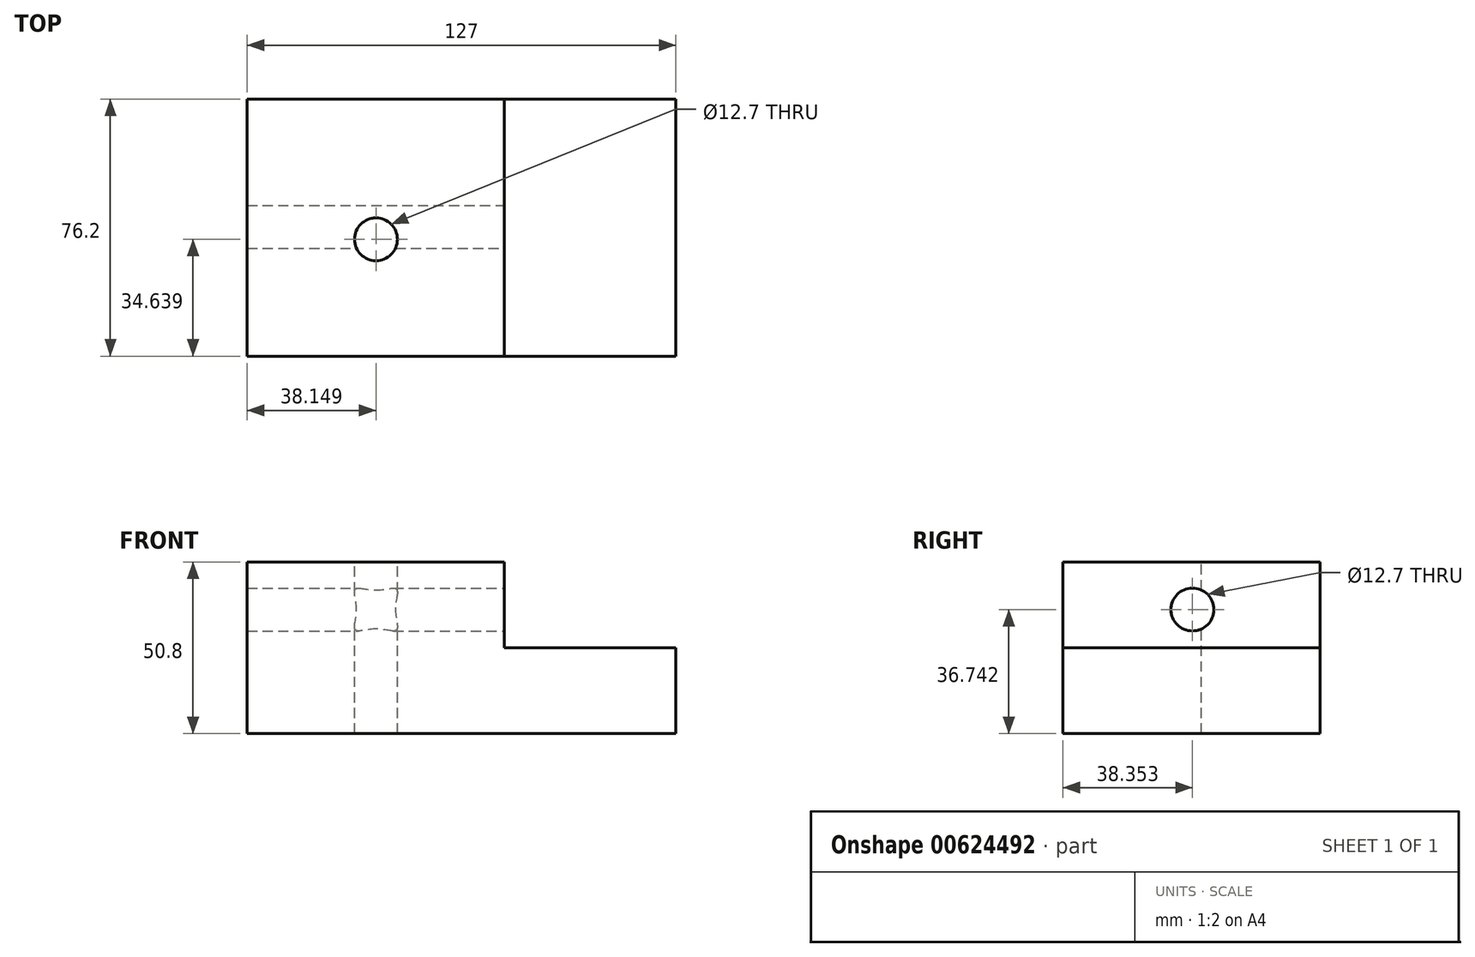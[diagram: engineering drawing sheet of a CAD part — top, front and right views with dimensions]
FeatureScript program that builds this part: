
annotation { "Feature Type Name" : "Feature", "Feature Type Description" : "" }
export const myFeature = defineFeature(function(context is Context, id is Id, definition is map)
    precondition{}
    {
        {
            var Q0;
            Q0=qCreatedBy(makeId("Front.planeOp"),FACE);
            var sketch = newSketch(context, id + "F0", { "sketchPlane" : qUnion([Q0])});
            skLineSegment(sketch, "E0.bottom", {"start": v(0, 0) * mm, "end": v(127, 0) * mm});
            skLineSegment(sketch, "E0.top", {"start": v(0, 50.8) * mm, "end": v(127, 50.8) * mm});
            skLineSegment(sketch, "E0.left", {"start": v(0, 0) * mm, "end": v(0, 50.8) * mm});
            skLineSegment(sketch, "E0.right", {"start": v(127, 0) * mm, "end": v(127, 50.8) * mm});
            skLineSegment(sketch, "E1.bottom", {"start": v(76.2, 50.8) * mm, "end": v(127, 50.8) * mm});
            skLineSegment(sketch, "E1.top", {"start": v(76.2, 25.4) * mm, "end": v(127, 25.4) * mm});
            skLineSegment(sketch, "E1.left", {"start": v(76.2, 50.8) * mm, "end": v(76.2, 25.4) * mm});
            skLineSegment(sketch, "E1.right", {"start": v(127, 50.8) * mm, "end": v(127, 25.4) * mm});
            skSolve(sketch);
        }
        {
            var Q0;
            Q0=makeQuery(id+"F0.imprint","IMPRINT",FACE,{"disambiguationData":[TD([[makeQuery(id+"F0.imprint","IMPRINT",EDGE,{"derivedFrom":sQuery(id+"F0.wireOp",EDGE,"E0.bottom")}),1.0]])]});
            extrude(context, id + "F1", {"entities" : qUnion([Q0]), "depth" : 76.2 * mm, "offsetDistance" : 25.4 * mm});
        }
        {
            var Q0;
            Q0=makeQuery(id+"F1.opExtrude","SWEPT_FACE",FACE,{"disambiguationData":[OSD([sQuery(id+"F0.wireOp",EDGE,"E0.top")])]});
            var sketch = newSketch(context, id + "F2", { "sketchPlane" : qUnion([Q0])});
            skCircle(sketch, "E2", {"center": v(38.15, -41.56) * mm, "radius": 15.37 * mm});
            skSolve(sketch);
        }
        {
            var Q0;
            Q0=sQuery(id+"F2.wireOp",VERTEX,"E2.center");
            var Q1;
            Q1=makeQuery(id+"F1.opExtrude","SWEPT_BODY",BODY,{"disambiguationData":[OSD([sQuery(id+"F0.wireOp",EDGE,"E0.bottom"),sQuery(id+"F0.wireOp",EDGE,"E0.top"),sQuery(id+"F0.wireOp",EDGE,"E0.left"),sQuery(id+"F0.wireOp",EDGE,"E0.right"),sQuery(id+"F0.wireOp",EDGE,"E1.top"),sQuery(id+"F0.wireOp",EDGE,"E1.left")])]});
            hole(context, id + "F3", {"style" : HoleStyle.SIMPLE, "endStyle" : HoleEndStyle.THROUGH, "holeDiameter" : 12.7 * mm, "majorDiameter" : 6.35 * mm, "isTappedThrough" : true, "tappedDepth" : 12.7 * mm, "tapClearance" : 3, "locations" : qUnion([Q0]), "scope" : qUnion([Q1])});
        }
        {
            var Q0;
            Q0=makeQuery(id+"F1.opExtrude","SWEPT_FACE",FACE,{"disambiguationData":[OSD([sQuery(id+"F0.wireOp",EDGE,"E1.left")])]});
            var sketch = newSketch(context, id + "F4", { "sketchPlane" : qUnion([Q0])});
            skCircle(sketch, "E3", {"center": v(-37.85, 36.74) * mm, "radius": 7.96 * mm});
            skSolve(sketch);
        }
        {
            var Q0;
            Q0=sQuery(id+"F4.wireOp",VERTEX,"E3.center");
            var Q1;
            Q1=makeQuery(id+"F1.opExtrude","SWEPT_BODY",BODY,{"disambiguationData":[OSD([sQuery(id+"F0.wireOp",EDGE,"E0.bottom"),sQuery(id+"F0.wireOp",EDGE,"E0.top"),sQuery(id+"F0.wireOp",EDGE,"E0.left"),sQuery(id+"F0.wireOp",EDGE,"E0.right"),sQuery(id+"F0.wireOp",EDGE,"E1.top"),sQuery(id+"F0.wireOp",EDGE,"E1.left")])]});
            hole(context, id + "F5", {"style" : HoleStyle.SIMPLE, "endStyle" : HoleEndStyle.THROUGH, "holeDiameter" : 12.7 * mm, "majorDiameter" : 6.35 * mm, "isTappedThrough" : true, "tappedDepth" : 12.7 * mm, "tapClearance" : 3, "locations" : qUnion([Q0]), "scope" : qUnion([Q1])});
        }
    });
